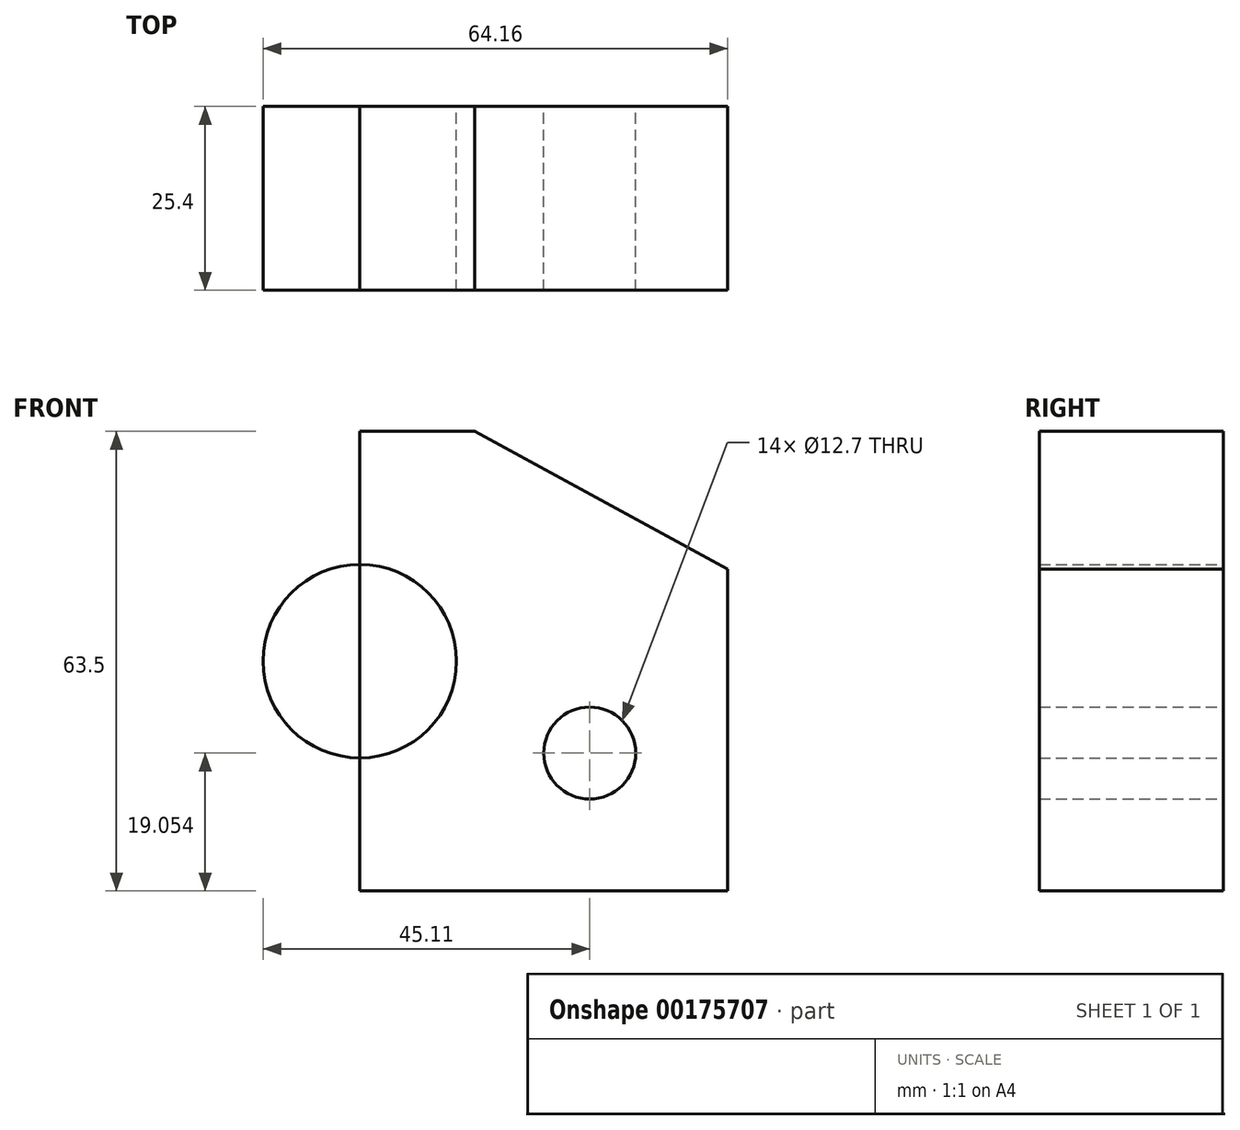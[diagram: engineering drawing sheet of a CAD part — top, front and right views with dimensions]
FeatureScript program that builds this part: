
annotation { "Feature Type Name" : "Feature", "Feature Type Description" : "" }
export const myFeature = defineFeature(function(context is Context, id is Id, definition is map)
    precondition{}
    {
        {
            var Q0;
            Q0=qCreatedBy(makeId("Front.planeOp"),FACE);
            var sketch = newSketch(context, id + "F0", { "sketchPlane" : qUnion([Q0])});
            skLineSegment(sketch, "E0", {"start": v(0, 15.07) * mm, "end": v(15.88, 15.07) * mm});
            skLineSegment(sketch, "E1", {"start": v(0, 15.07) * mm, "end": v(0, -48.43) * mm});
            skLineSegment(sketch, "E2", {"start": v(0, -48.43) * mm, "end": v(50.8, -48.43) * mm});
            skLineSegment(sketch, "E3", {"start": v(50.8, -48.43) * mm, "end": v(50.8, -3.98) * mm});
            skLineSegment(sketch, "E4", {"start": v(15.88, 15.07) * mm, "end": v(50.8, -3.98) * mm});
            skArc(sketch, "E5", {"start": v(0, -30.03) * mm, "mid": v(13.36, -16.68) * mm, "end": v(0, -3.32) * mm});
            skCircle(sketch, "E6", {"center": v(31.75, -29.38) * mm, "radius": 6.35 * mm});
            skArc(sketch, "E7.MirrorCS", {"start": v(0, -30.03) * mm, "mid": v(-13.36, -16.68) * mm, "end": v(0, -3.32) * mm});
            skLineSegment(sketch, "E8.MirrorCS", {"start": v(0, 15.07) * mm, "end": v(-15.88, 15.07) * mm});
            skLineSegment(sketch, "E9.MirrorCS", {"start": v(-15.88, 15.07) * mm, "end": v(-50.8, -3.98) * mm});
            skLineSegment(sketch, "E10.MirrorCS", {"start": v(-50.8, -48.43) * mm, "end": v(-50.8, -3.98) * mm});
            skLineSegment(sketch, "E11.MirrorCS", {"start": v(0, -48.43) * mm, "end": v(-50.8, -48.43) * mm});
            skCircle(sketch, "E12.MirrorC", {"center": v(-31.75, -29.38) * mm, "radius": 6.35 * mm});
            skSolve(sketch);
        }
        {
            var Q0;
            {var subQ3=sQuery(id+"F0.wireOp",EDGE,"E7.MirrorCS");Q0=makeQuery(id+"F0.imprint","IMPRINT",FACE,{"disambiguationData":[TD([[makeQuery(id+"F0.imprint","IMPRINT",EDGE,{"derivedFrom":subQ3}),1.0]])]});}
            var Q1;
            {var subQ4=sQuery(id+"F0.wireOp",EDGE,"E0");Q1=makeQuery(id+"F0.imprint","IMPRINT",FACE,{"disambiguationData":[TD([[makeQuery(id+"F0.imprint","IMPRINT",EDGE,{"derivedFrom":subQ4}),-1.0]])]});}
            extrude(context, id + "F1", {"entities" : qUnion([Q0, Q1]), "depth" : 25.4 * mm});
        }
    });
